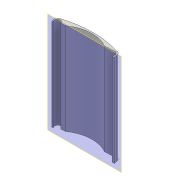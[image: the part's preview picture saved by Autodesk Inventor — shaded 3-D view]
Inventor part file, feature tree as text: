
AUTODESK INVENTOR PART (.ipt)
format: ipt  version: 2021 (Build 250183000, 183)  size: 115,712 bytes
history: native  units: mm
features: extrude x1, plane x1, split x1, sketch x1
ambient origin geometry x8: Origin, YZ Plane, XZ Plane, XY Plane, X Axis, Y Axis, Z Axis, Center Point
bodies: Solid1 (feature_tree)
feature tree (4):
  extrude  "Extrusion1"  Depth=27.0mm
  plane  "Work Plane1"
  split  "Split1"
  sketch  "Sketch1"  dims[d0=6.2mm d1=6.2mm d6=9.0mm d7=9.0mm d8=135.0deg d9=75.0mm d11=100.0mm d12=100.0mm d13=100.0mm d14=0.0mm d15=27.0mm]
